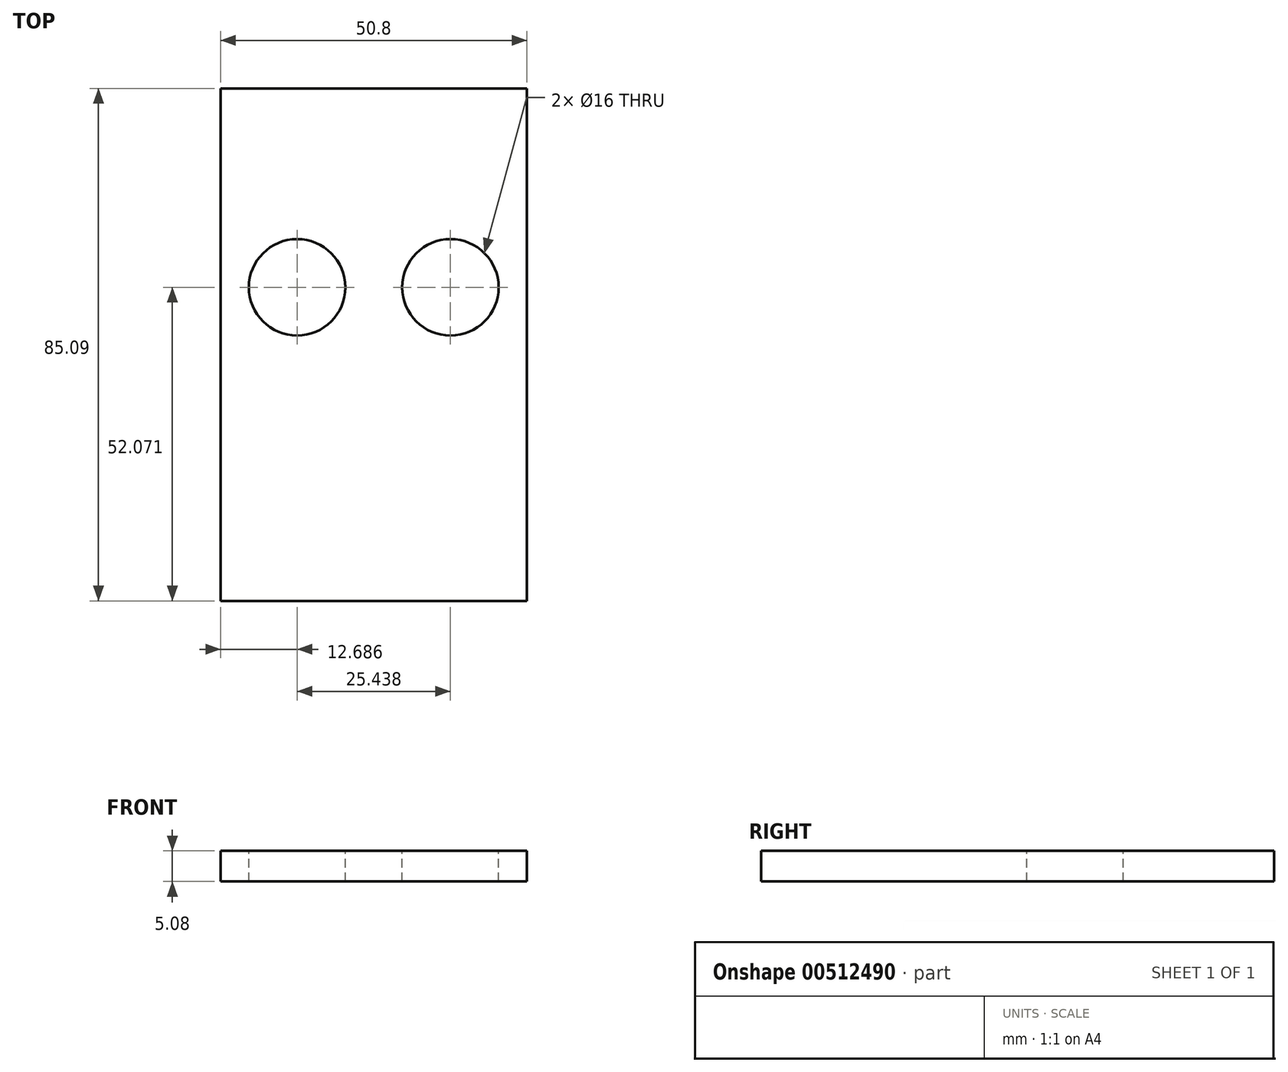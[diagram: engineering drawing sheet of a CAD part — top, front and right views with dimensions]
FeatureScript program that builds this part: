
annotation { "Feature Type Name" : "Feature", "Feature Type Description" : "" }
export const myFeature = defineFeature(function(context is Context, id is Id, definition is map)
    precondition{}
    {
        {
            var Q0;
            Q0=qCreatedBy(makeId("Top.planeOp"),FACE);
            var sketch = newSketch(context, id + "F0", { "sketchPlane" : qUnion([Q0])});
            skLineSegment(sketch, "E0.bottom", {"start": v(-21.7, 66.83) * mm, "end": v(29.1, 66.83) * mm});
            skLineSegment(sketch, "E0.top", {"start": v(-21.7, -18.26) * mm, "end": v(29.1, -18.26) * mm});
            skLineSegment(sketch, "E0.left", {"start": v(-21.7, 66.83) * mm, "end": v(-21.7, -18.26) * mm});
            skLineSegment(sketch, "E0.right", {"start": v(29.1, 66.83) * mm, "end": v(29.1, -18.26) * mm});
            skSolve(sketch);
        }
        {
            var Q0;
            Q0=qSketchRegion(id+"F0",true);
            var Q1;
            Q1=makeQuery(id+"F0.imprint","IMPRINT",FACE,{"disambiguationData":[TD([[makeQuery(id+"F0.imprint","IMPRINT",EDGE,{"derivedFrom":sQuery(id+"F0.wireOp",EDGE,"E0.bottom")}),-1.0]])]});
            extrude(context, id + "F1", {"entities" : qUnion([Q0, Q1]), "depth" : 5.08 * mm});
        }
        {
            var Q0;
            Q0=makeQuery(id+"F1.opExtrude","CAP_FACE",FACE,{"disambiguationData":[OSD([sQuery(id+"F0.wireOp",EDGE,"E0.bottom"),sQuery(id+"F0.wireOp",EDGE,"E0.top"),sQuery(id+"F0.wireOp",EDGE,"E0.left"),sQuery(id+"F0.wireOp",EDGE,"E0.right")])],"isStart":false});
            var sketch = newSketch(context, id + "F2", { "sketchPlane" : qUnion([Q0])});
            skCircle(sketch, "E1", {"center": v(-9.01, 33.81) * mm, "radius": 8 * mm});
            skCircle(sketch, "E2", {"center": v(16.42, 33.81) * mm, "radius": 8 * mm});
            skSolve(sketch);
        }
        {
            var Q0;
            Q0=makeQuery(id+"F2.imprint","IMPRINT",FACE,{"disambiguationData":[TD([[makeQuery(id+"F2.imprint","IMPRINT",EDGE,{"derivedFrom":sQuery(id+"F2.wireOp",EDGE,"E2")}),1.0]])]});
            var Q1;
            Q1=makeQuery(id+"F2.imprint","IMPRINT",FACE,{"disambiguationData":[TD([[makeQuery(id+"F2.imprint","IMPRINT",EDGE,{"derivedFrom":sQuery(id+"F2.wireOp",EDGE,"E1")}),1.0]])]});
            extrude(context, id + "F3", {"entities" : qUnion([Q0, Q1]), "operationType" : NewBodyOperationType.REMOVE, "oppositeDirection" : true, "depth" : 25.4 * mm});
        }
    });
